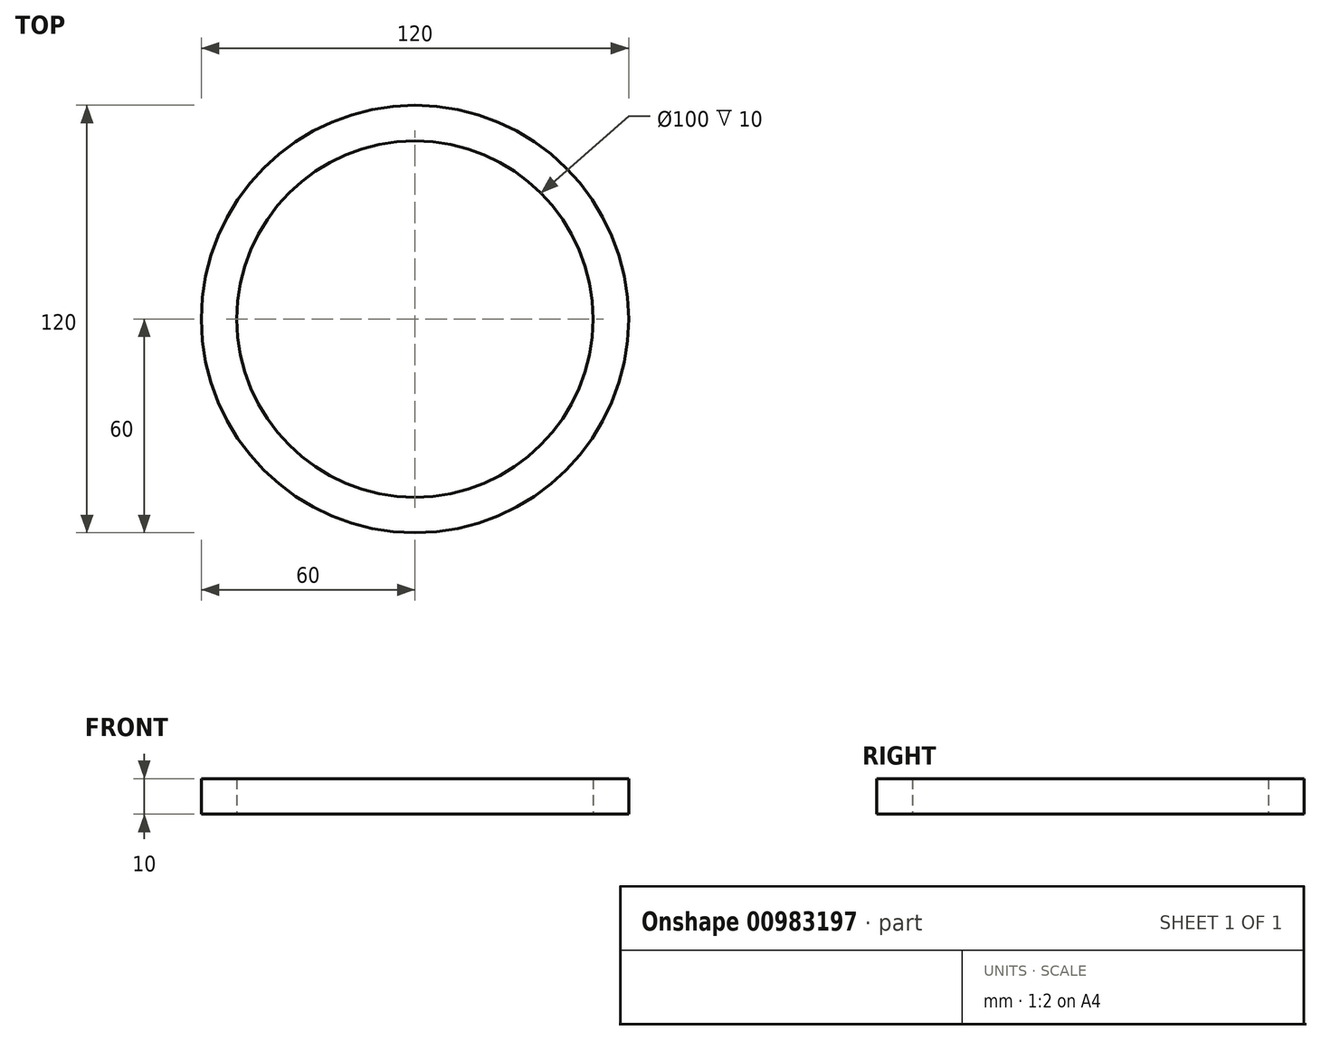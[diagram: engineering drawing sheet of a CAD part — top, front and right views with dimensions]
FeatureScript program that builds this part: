
annotation { "Feature Type Name" : "Feature", "Feature Type Description" : "" }
export const myFeature = defineFeature(function(context is Context, id is Id, definition is map)
    precondition{}
    {
        {
            var Q0;
            Q0=qCreatedBy(makeId("Top.planeOp"),FACE);
            var sketch = newSketch(context, id + "F0", { "sketchPlane" : qUnion([Q0])});
            skCircle(sketch, "E0", {"center": v(0, 0) * mm, "radius": 50 * mm});
            skCircle(sketch, "E1", {"center": v(0, 0) * mm, "radius": 60 * mm});
            skSolve(sketch);
        }
        {
            var Q0;
            Q0 = qSketchRegion(id + "F0", true);
            extrude(context, id + "F1", {"entities" : qUnion([Q0]), "depth" : 10 * mm, "offsetDistance" : 25 * mm});
        }
    });
